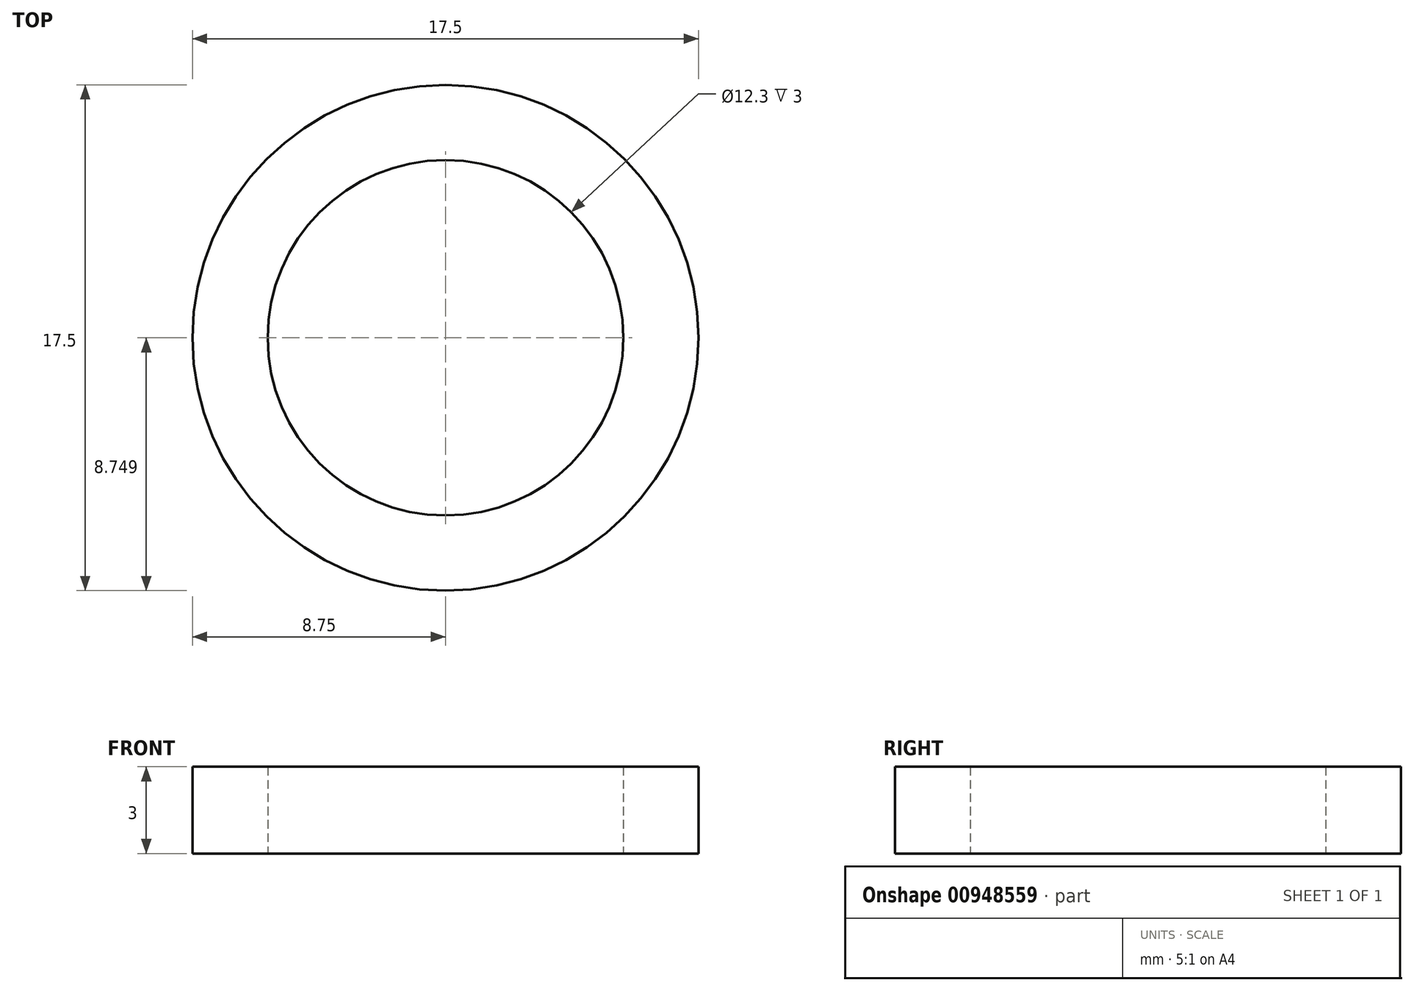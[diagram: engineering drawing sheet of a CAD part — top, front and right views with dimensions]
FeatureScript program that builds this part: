
annotation { "Feature Type Name" : "Feature", "Feature Type Description" : "" }
export const myFeature = defineFeature(function(context is Context, id is Id, definition is map)
    precondition{}
    {
        {
            var Q0;
            Q0=qCreatedBy(makeId("Top.planeOp"),FACE);
            var sketch = newSketch(context, id + "F0", { "sketchPlane" : qUnion([Q0])});
            skCircle(sketch, "E0", {"center": v(-89.14, 24.94) * mm, "radius": 6.15 * mm});
            skCircle(sketch, "E1.0", {"center": v(-89.14, 24.94) * mm, "radius": 8.75 * mm});
            skSolve(sketch);
        }
        {
            var Q0;
            Q0=makeQuery(id+"F0.imprint","IMPRINT",FACE,{"disambiguationData":[TD([[makeQuery(id+"F0.imprint","IMPRINT",EDGE,{"derivedFrom":sQuery(id+"F0.wireOp",EDGE,"E0")}),-1.0]])]});
            extrude(context, id + "F1", {"entities" : qUnion([Q0]), "depth" : 3 * mm, "offsetDistance" : 25 * mm});
        }
    });
